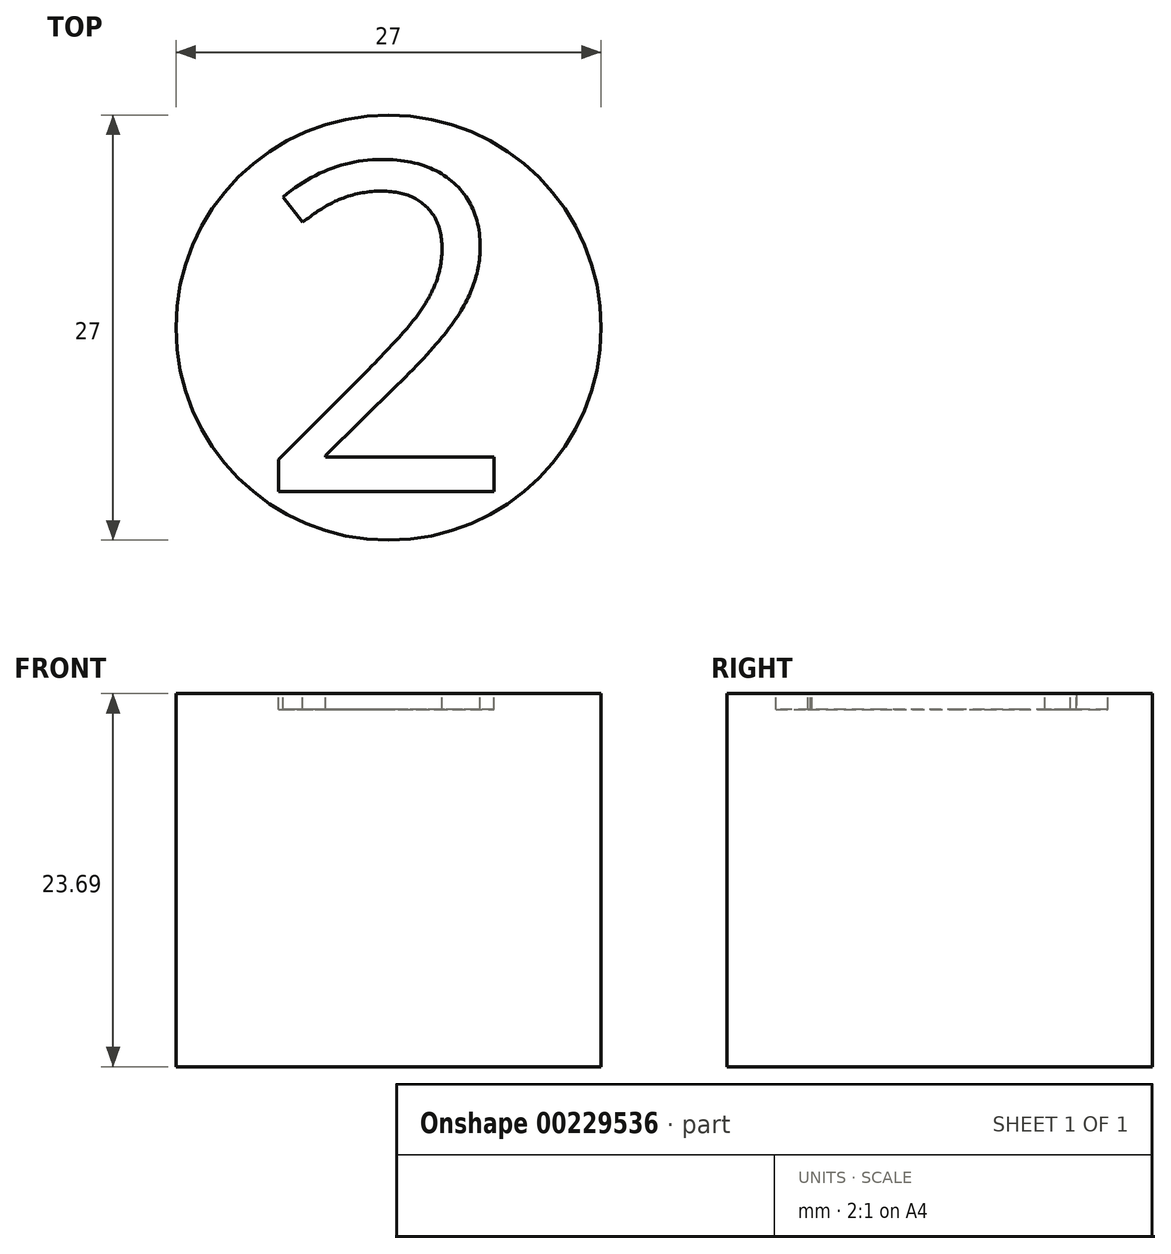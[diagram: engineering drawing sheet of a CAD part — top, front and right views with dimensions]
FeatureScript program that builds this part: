
annotation { "Feature Type Name" : "Feature", "Feature Type Description" : "" }
export const myFeature = defineFeature(function(context is Context, id is Id, definition is map)
    precondition{}
    {
        {
            assignVariable(context, id + "F0", {"name" : "TotalHeight", "anyValue" : 66.04});
        }
        {
            var Q0;
            Q0=qCreatedBy(makeId("Top.planeOp"),FACE);
            var sketch = newSketch(context, id + "F1", { "sketchPlane" : qUnion([Q0])});
            skCircle(sketch, "E0", {"center": v(0, 0) * mm, "radius": 13.5 * mm});
            skSolve(sketch);
        }
        {
            var Q0;
            Q0=makeQuery(id+"F1.imprint","IMPRINT",FACE,{"disambiguationData":[TD([[makeQuery(id+"F1.imprint","IMPRINT",EDGE,{"derivedFrom":sQuery(id+"F1.wireOp",EDGE,"E0")}),1.0]])]});
            extrude(context, id + "F2", {"entities" : qUnion([Q0]), "depth" : (getVariable(context, 'TotalHeight') - 42.35) * mm});
        }
        {
            var Q0;
            Q0=makeQuery(id+"F2.opExtrude","CAP_FACE",FACE,{"disambiguationData":[OSD([sQuery(id+"F1.wireOp",EDGE,"E0")])],"isStart":false});
            var sketch = newSketch(context, id + "F3", { "sketchPlane" : qUnion([Q0])});
            skText(sketch, "E1", { "text": "2", "fontName": "OpenSans-Regular.ttf"});
            const initialGuessF3  = {"E1": [-0.0084, -0.01041, 1, 0, 0.02098]};
            skSetInitialGuess(sketch, initialGuessF3);
            skSolve(sketch);
        }
        {
            var Q0;
            Q0 = qSketchRegion(id + "F3", true);
            extrude(context, id + "F4", {"entities" : qUnion([Q0]), "operationType" : NewBodyOperationType.REMOVE, "oppositeDirection" : true, "depth" : 1 * mm});
        }
    });
